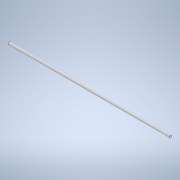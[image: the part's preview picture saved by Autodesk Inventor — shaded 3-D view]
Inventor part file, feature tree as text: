
AUTODESK INVENTOR PART (.ipt)
format: ipt  version: 2020.1 (Build 241239000, 239)  size: 99,840 bytes
history: native  units: mm
features: extrude x3, sketch x3
ambient origin geometry x8: Origin, YZ Plane, XZ Plane, XY Plane, X Axis, Y Axis, Z Axis, Center Point
bodies: Solid1 (feature_tree)
feature tree (6):
  extrude  "Extrusion1"  Depth=165.1mm TaperAngle=0.0deg
  extrude  "Extrusion2"  Depth=20.32mm TaperAngle=0.0deg
  extrude  "Extrusion3"  [1 undecoded]
  sketch  "Sketch1"  dims[d0=3.175mm d1=165.1mm d2=0.0mm]
  sketch  "Sketch2"  dims[d3=20.32mm d4=0.0mm d5=20.32mm d6=0.0mm]
  sketch  "Sketch3"
note: 1 required parameter value undecoded (feature->parameter linkage not recoverable at this tier; creation-order binding heuristic only, values carry confidence <= 0.55)
